# Revit family: Atdec-Wallmount-AD-WFP50-Portrait-
name_source: partatom
category: Generic Models
revit_build: Autodesk Revit 2016 (Build: 20150220_1215(x64)
units: mm (PartAtom-declared; Revit-internal decimal feet)

## family parameters
Can host rebar = No
Cut with Voids When Loaded = No
Host = Face
Part Type = Normal
Room Calculation Point = No
Round Connector Dimension = Use Diameter
Shared = No

## types (1)
- AD-WFP-5040
    Assembly Code = E1010800
    Colour Options = Black
    Default Elevation = 1219 mm
    Description = Fixed angle portriat wall mount VESA up to 400x600
    Flat screen maximum supported weight = 50kg (110lb)
    Manufacturer = Atdec
    Master Carton Dimensions = 677mm (26.7") Length, 335mm (13.2") Width, 185mm (7.3") Height
    Material = Steel
    Maximum distance from wall (mm) = 27mm (1.06")
    Minimum distance from wall (mm) = 27mm (1.06")
    Model = AD-WFP-5040
    Pan Adjustment = -
    Plate Width = 448 mm  [stored 1.46982 ft]
    Product Family = Wall Mount Rail
    Product Information Link = https://www.atdec.com.au
    Range of Motion = Fixed Angle
    Security feature = Can be secured with padlock (not included)
    Single Unit Dimensions = 660mm (26") Length, 156mm (6.1") Width, 41mm (1.6") Height
    Single units per master pack = 8
    Tilt Adjustment = -
    UPC Code = 881493019263
    URL = www.atdec.com.au
    Universal Height (mm) = From 100 to 600
    Universal Width (mm) = From 100 to 400
    VESA mounting hole pattern, mm = 100x100, 100x200, 200x100, 200x200, 200x300, 200x400, 300x200, 300x300, 400x200, 400x300, 400x400
    Warranty = 10 years
    Weight, Single Unit = 2.08 (4.59lb)
    Weight, master carton = 17.4kg (38.36lb)

note: [stored X ft] marks values corroborated as IEEE doubles in the binary element streams (Revit-internal decimal feet)

## geometry (parser evidence)
native form markers: Sweep x2
no freeform markers — native parametric forms only
